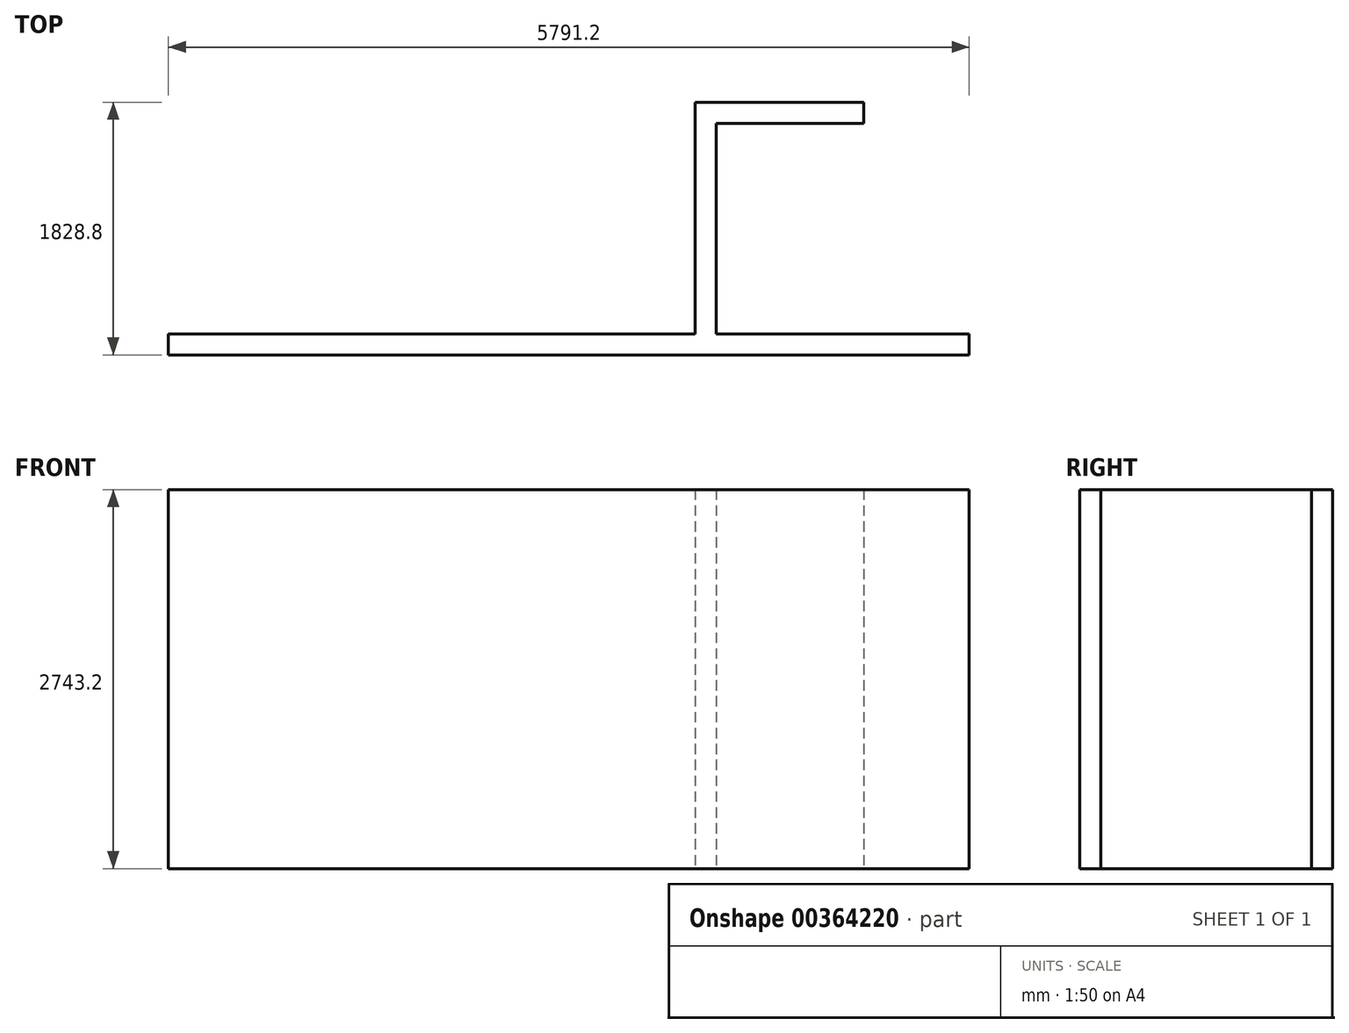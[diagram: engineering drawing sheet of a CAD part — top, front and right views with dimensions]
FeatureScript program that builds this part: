
annotation { "Feature Type Name" : "Feature", "Feature Type Description" : "" }
export const myFeature = defineFeature(function(context is Context, id is Id, definition is map)
    precondition{}
    {
        {
            var Q0;
            Q0=qCreatedBy(makeId("Top.planeOp"),FACE);
            var sketch = newSketch(context, id + "F0", { "sketchPlane" : qUnion([Q0])});
            skLineSegment(sketch, "E0.bottom", {"start": v(0, 0) * mm, "end": v(5791.2, 0) * mm});
            skLineSegment(sketch, "E0.top", {"start": v(0, 152.4) * mm, "end": v(3810, 152.4) * mm});
            skLineSegment(sketch, "E0.left", {"start": v(0, 0) * mm, "end": v(0, 152.4) * mm});
            skLineSegment(sketch, "E0.right", {"start": v(5791.2, 0) * mm, "end": v(5791.2, 152.4) * mm});
            skLineSegment(sketch, "E1.left", {"start": v(3810, 152.4) * mm, "end": v(3810, 1828.8) * mm});
            skLineSegment(sketch, "E1.right", {"start": v(3962.4, 152.4) * mm, "end": v(3962.4, 1676.4) * mm});
            skLineSegment(sketch, "E2.trimOffspring", {"start": v(3962.4, 152.4) * mm, "end": v(5791.2, 152.4) * mm});
            skLineSegment(sketch, "E3.bottom", {"start": v(3810, 1828.8) * mm, "end": v(5029.2, 1828.8) * mm});
            skLineSegment(sketch, "E3.top", {"start": v(3962.4, 1676.4) * mm, "end": v(5029.2, 1676.4) * mm});
            skLineSegment(sketch, "E3.right", {"start": v(5029.2, 1828.8) * mm, "end": v(5029.2, 1676.4) * mm});
            skSolve(sketch);
        }
        {
            var Q0;
            Q0 = qSketchRegion(id + "F0", true);
            extrude(context, id + "F1", {"entities" : qUnion([Q0]), "depth" : 2743.2 * mm});
        }
    });
